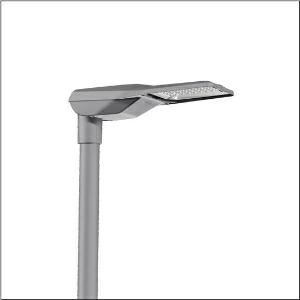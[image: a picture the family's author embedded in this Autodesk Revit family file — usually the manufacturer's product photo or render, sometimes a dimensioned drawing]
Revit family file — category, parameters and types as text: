
# Revit family: streetlight_sl_21_mini___st0_8a_5xe6c43a08hb_ef0f
name_source: partatom
category: Lighting Fixtures
units: mm (PartAtom-declared; Revit-internal decimal feet)

## family parameters
Cut with Voids When Loaded = No
Host = Face
Light Source = No
Part Type = Normal
Room Calculation Point = No
Round Connector Dimension = Use Diameter
Shared = No

## types (1)
- --- (1 x LED, 9430 lm, 66 W, 4000K)
    Apparent Load = 66 VA
    CIE Flux Codes = 38 75 97 100 100
    Color Rendering = 70
    Color Temperature = 4000K
    Default Elevation = 1800 mm
    Description = Streetlight SL 21 mini, mast luminaire, primary light control with lens, of PMMA, primary optical cover: cover, of toughened safety glass, transparent, light distribution: ST0.8a, light emission: direct distribution, primary light characteristic: asymmetric, installation type: post-top, side-entry, LED, 3G 1.5mm², High Power LED, rated luminous flux: 9.430lm, luminous efficacy: 143lm/W, light colour: 740, colour temperature: 4000K, control: overheat protection, constant luminous flux control, time-dependent luminous flux control, flexible luminous flux parameterisation, mains connection: 230..240V, AC, 50/60Hz, connection cable pre-assembled, cable length: 8,5m, wiring characteristics: H07RN-F, start of lifetime: 66W, end of service life: 69W, reduction: 30W, luminaire housing, of diecast aluminium, powder-coated, Siteco® metallic grey (DB 702S), corrosivity category C5 mid according to DIN EN ISO 12944, please order mast flange separately, inclination adjustable: 0°, 5°, 10°, 15°, sealing non-destructively replaceable, multi-level sealing system, length: 628mm, width: 235mm, height: 110mm, mast flange for spigot size: 42mm (side-entry): 5XC10008XM4, 60/48mm (side-entry/post-top): 5XC10108XM2, 76/60mm (side-entry/post-top): 5XC10108XM1, protection rating (complete): IP66, insulation class (complete): insulation class II (safety insulation), certification: CE, ENEC, ENEC+, VDE, impact resistance: IK09, permissible operating ambient temperature for outdoor applications: -40..+50°C, standard-compliant lighting for roads and squares, packaging unit: 1 piece

Light Distribution: ST0.8a
    Height = 110 mm
    Lamp = 1 x LED
    Lamp Light Flux = 9430 lm
    Lamp Power = 66 W
    Lamp count = 1
    Length = 625 mm
    Luminous efficacy = 143 lm/W
    Manufacturer = Siteco
    ModVariant = No
    Model = 5XE6C43A08HB
    Number of Poles = 1
    OnlyDefault = Yes
    Power Factor = 1
    Product Name = Streetlight SL 21 mini | ST0.8a
    Product group = mast luminaire | pylon top
    ProductGroupID = 6100
    Protection Class = Protection class II
    Protection Degree = IP 66
    RLX_Detail_Level = 1
    RLX_Emergency_Light_Flux = 0 lm
    RLX_Emergency_Type = 0
    RLX_Emergency_Type_DB = No
    RlxData = <blob elided: 92205 chars, md5=938dec26>
    Socket = socket
    Standby Power = 0 W
    System Light Flux = 9430 lm
    System Power = 66 W
    Type Comments = factory setting: luminous flux: 100 % | Output Level: 100 % | 670 mA
    Type Image = l_1003519.jpg
    URL = http://relux.com
    VarID = @adj_136651
    Voltage = 0 V
    Weight = 0.00 kg
    Width = 234 mm

## geometry (parser evidence)
native form markers: Blend x4, Sweep x13
no freeform markers — native parametric forms only
